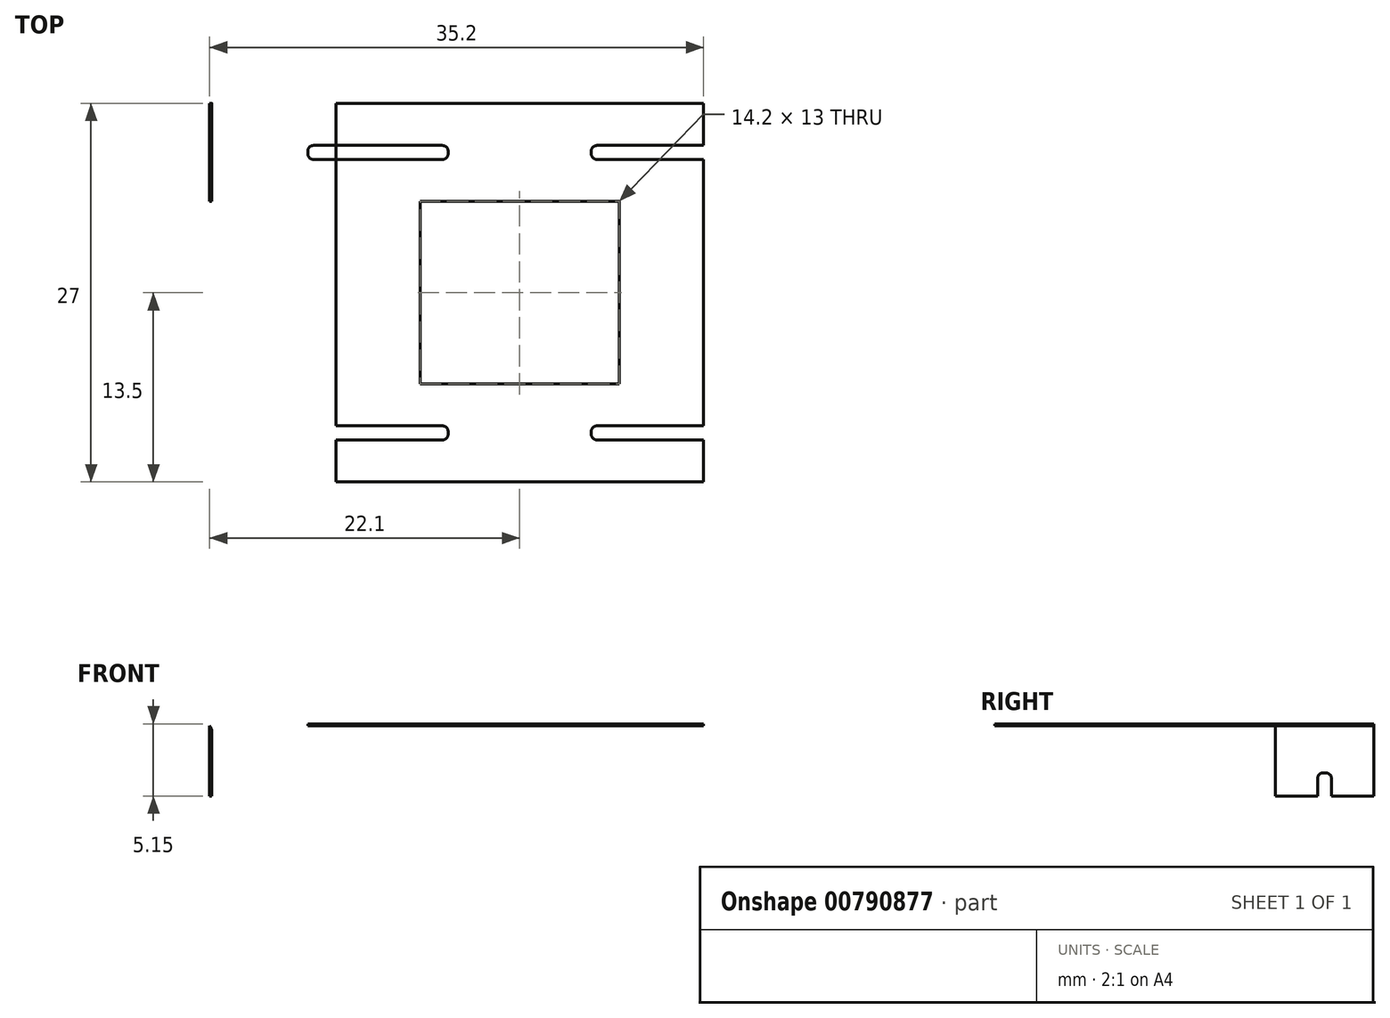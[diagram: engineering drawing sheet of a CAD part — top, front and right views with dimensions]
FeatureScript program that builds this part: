
annotation { "Feature Type Name" : "Feature", "Feature Type Description" : "" }
export const myFeature = defineFeature(function(context is Context, id is Id, definition is map)
    precondition{}
    {
        {
            var Q0;
            Q0=qCreatedBy(makeId("Top.planeOp"),FACE);
            var sketch = newSketch(context, id + "F0", { "sketchPlane" : qUnion([Q0])});
            skLineSegment(sketch, "E0.bottom", {"start": v(7.1, 6.5) * mm, "end": v(-7.1, 6.5) * mm});
            skLineSegment(sketch, "E0.top", {"start": v(7.1, -6.5) * mm, "end": v(-7.1, -6.5) * mm});
            skLineSegment(sketch, "E0.left", {"start": v(7.1, 6.5) * mm, "end": v(7.1, -6.5) * mm});
            skLineSegment(sketch, "E0.right", {"start": v(-7.1, 6.5) * mm, "end": v(-7.1, -6.5) * mm});
            skPoint(sketch, "E0.middle", {"position": v(0, 0) * mm});
            skLineSegment(sketch, "E1", {"start": v(13.1, 13.5) * mm, "end": v(13.1, 10.5) * mm});
            skLineSegment(sketch, "E2", {"start": v(13.1, 13.5) * mm, "end": v(-7.1, 13.5) * mm});
            skLineSegment(sketch, "E3.bottom", {"start": v(5.5, 9.5) * mm, "end": v(14.7, 9.5) * mm});
            skLineSegment(sketch, "E3.top", {"start": v(5.5, 10.5) * mm, "end": v(14.7, 10.5) * mm});
            skLineSegment(sketch, "E3.left", {"start": v(5.1, 9.9) * mm, "end": v(5.1, 10.1) * mm});
            skLineSegment(sketch, "E3.right", {"start": v(15.1, 9.9) * mm, "end": v(15.1, 10.1) * mm});
            skPoint(sketch, "E3.middle", {"position": v(10.1, 10) * mm});
            skPoint(sketch, "E4.visualSharp", {"position": v(5.1, 10.5) * mm});
            skArc(sketch, "E4.filletArc", {"start": v(5.5, 10.5) * mm, "mid": v(5.22, 10.38) * mm, "end": v(5.1, 10.1) * mm});
            skPoint(sketch, "E5.visualSharp", {"position": v(5.1, 9.5) * mm});
            skArc(sketch, "E5.filletArc", {"start": v(5.1, 9.9) * mm, "mid": v(5.22, 9.62) * mm, "end": v(5.5, 9.5) * mm});
            skPoint(sketch, "E6.visualSharp", {"position": v(15.1, 10.5) * mm});
            skArc(sketch, "E6.filletArc", {"start": v(15.1, 10.1) * mm, "mid": v(14.98, 10.38) * mm, "end": v(14.7, 10.5) * mm});
            skPoint(sketch, "E7.visualSharp", {"position": v(15.1, 9.5) * mm});
            skArc(sketch, "E7.filletArc", {"start": v(14.7, 9.5) * mm, "mid": v(14.98, 9.62) * mm, "end": v(15.1, 9.9) * mm});
            skLineSegment(sketch, "E8.trimOffspring", {"start": v(13.1, 9.5) * mm, "end": v(13.1, 0) * mm});
            skArc(sketch, "E9.MirrorCS", {"start": v(-5.5, 10.5) * mm, "mid": v(-5.22, 10.38) * mm, "end": v(-5.1, 10.1) * mm});
            skArc(sketch, "E10.MirrorCS", {"start": v(-15.1, 10.1) * mm, "mid": v(-14.98, 10.38) * mm, "end": v(-14.7, 10.5) * mm});
            skLineSegment(sketch, "E11.MirrorCS", {"start": v(-15.1, 9.9) * mm, "end": v(-15.1, 10.1) * mm});
            skArc(sketch, "E12.MirrorCS", {"start": v(-14.7, 9.5) * mm, "mid": v(-14.98, 9.62) * mm, "end": v(-15.1, 9.9) * mm});
            skArc(sketch, "E13.MirrorCS", {"start": v(-5.1, 9.9) * mm, "mid": v(-5.22, 9.62) * mm, "end": v(-5.5, 9.5) * mm});
            skLineSegment(sketch, "E14.MirrorCS", {"start": v(-5.1, 9.9) * mm, "end": v(-5.1, 10.1) * mm});
            skPoint(sketch, "E15.MirrorP", {"position": v(-5.1, 9.5) * mm});
            skLineSegment(sketch, "E16.MirrorCS", {"start": v(-5.5, 10.5) * mm, "end": v(-14.7, 10.5) * mm});
            skPoint(sketch, "E17.MirrorP", {"position": v(-10.1, 10) * mm});
            skLineSegment(sketch, "E18.MirrorCS", {"start": v(-5.5, 9.5) * mm, "end": v(-14.7, 9.5) * mm});
            skPoint(sketch, "E19.MirrorP", {"position": v(-15.1, 10.5) * mm});
            skLineSegment(sketch, "E20.MirrorCS", {"start": v(-13.1, 9.5) * mm, "end": v(-13.1, 0) * mm});
            skPoint(sketch, "E21.MirrorP", {"position": v(-5.1, 10.5) * mm});
            skLineSegment(sketch, "E22.MirrorCS", {"start": v(-13.1, 13.5) * mm, "end": v(-13.1, 10.5) * mm});
            skPoint(sketch, "E23.MirrorP", {"position": v(-15.1, 9.5) * mm});
            skLineSegment(sketch, "E24", {"start": v(-13.1, 13.5) * mm, "end": v(-7.1, 13.5) * mm});
            skLineSegment(sketch, "E25.bottom", {"start": v(-13.1, 13.5) * mm, "end": v(-22.1, 13.5) * mm});
            skLineSegment(sketch, "E25.top", {"start": v(-13.1, 6.5) * mm, "end": v(-22.1, 6.5) * mm});
            skLineSegment(sketch, "E25.left", {"start": v(-13.1, 13.5) * mm, "end": v(-13.1, 6.5) * mm});
            skLineSegment(sketch, "E25.right", {"start": v(-22.1, 13.5) * mm, "end": v(-22.1, 6.5) * mm});
            skArc(sketch, "E26.MirrorCS", {"start": v(14.7, -9.5) * mm, "mid": v(14.98, -9.62) * mm, "end": v(15.1, -9.9) * mm});
            skLineSegment(sketch, "E27.MirrorCS", {"start": v(15.1, -9.9) * mm, "end": v(15.1, -10.1) * mm});
            skArc(sketch, "E28.MirrorCS", {"start": v(15.1, -10.1) * mm, "mid": v(14.98, -10.38) * mm, "end": v(14.7, -10.5) * mm});
            skLineSegment(sketch, "E29.MirrorCS", {"start": v(13.1, -13.5) * mm, "end": v(13.1, -10.5) * mm});
            skLineSegment(sketch, "E30.MirrorCS", {"start": v(13.1, -9.5) * mm, "end": v(13.1, 0) * mm});
            skLineSegment(sketch, "E31.MirrorCS", {"start": v(13.1, -13.5) * mm, "end": v(-7.1, -13.5) * mm});
            skLineSegment(sketch, "E32.MirrorCS", {"start": v(5.5, -10.5) * mm, "end": v(14.7, -10.5) * mm});
            skPoint(sketch, "E33.MirrorP", {"position": v(15.1, -9.5) * mm});
            skPoint(sketch, "E34.MirrorP", {"position": v(15.1, -10.5) * mm});
            skPoint(sketch, "E35.MirrorP", {"position": v(10.1, -10) * mm});
            skLineSegment(sketch, "E36.MirrorCS", {"start": v(5.5, -9.5) * mm, "end": v(14.7, -9.5) * mm});
            skLineSegment(sketch, "E37.MirrorCS", {"start": v(5.1, -9.9) * mm, "end": v(5.1, -10.1) * mm});
            skArc(sketch, "E38.MirrorCS", {"start": v(5.1, -9.9) * mm, "mid": v(5.22, -9.62) * mm, "end": v(5.5, -9.5) * mm});
            skArc(sketch, "E39.MirrorCS", {"start": v(5.5, -10.5) * mm, "mid": v(5.22, -10.38) * mm, "end": v(5.1, -10.1) * mm});
            skPoint(sketch, "E40.MirrorP", {"position": v(5.1, -10.5) * mm});
            skPoint(sketch, "E41.MirrorP", {"position": v(5.1, -9.5) * mm});
            skArc(sketch, "E42.MirrorCS", {"start": v(-5.1, -9.9) * mm, "mid": v(-5.22, -9.62) * mm, "end": v(-5.5, -9.5) * mm});
            skArc(sketch, "E43.MirrorCS", {"start": v(-5.5, -10.5) * mm, "mid": v(-5.22, -10.38) * mm, "end": v(-5.1, -10.1) * mm});
            skLineSegment(sketch, "E44.MirrorCS", {"start": v(-5.1, -9.9) * mm, "end": v(-5.1, -10.1) * mm});
            skPoint(sketch, "E45.MirrorP", {"position": v(-5.1, -10.5) * mm});
            skLineSegment(sketch, "E46.MirrorCS", {"start": v(-5.5, -10.5) * mm, "end": v(-13.1, -10.5) * mm});
            skPoint(sketch, "E47.MirrorP", {"position": v(-10.1, -10) * mm});
            skPoint(sketch, "E48.MirrorP", {"position": v(-5.1, -9.5) * mm});
            skLineSegment(sketch, "E49.MirrorCS", {"start": v(-5.5, -9.5) * mm, "end": v(-13.1, -9.5) * mm});
            skLineSegment(sketch, "E50.MirrorCS", {"start": v(-13.1, -13.5) * mm, "end": v(-13.1, -10.5) * mm});
            skLineSegment(sketch, "E51.MirrorCS", {"start": v(-13.1, -13.5) * mm, "end": v(-7.1, -13.5) * mm});
            skLineSegment(sketch, "E52.MirrorCS", {"start": v(-13.1, -9.5) * mm, "end": v(-13.1, 0) * mm});
            skLineSegment(sketch, "E53.direction1", {"start": v(-7.1, -13.5) * mm, "end": v(13.1, -13.5) * mm, "construction": true});
            skPoint(sketch, "E54.orphan", {"position": v(-14.7, -9.5) * mm});
            skPoint(sketch, "E55.orphan", {"position": v(-14.7, -10.5) * mm});
            skLineSegment(sketch, "E56.trimOffspring", {"start": v(-13.1, -9.5) * mm, "end": v(-13.1, -6.5) * mm});
            skSolve(sketch);
        }
        {
            var Q0;
            {var subQ5=sQuery(id+"F0.wireOp",EDGE,"E10.MirrorCS");Q0=makeQuery(id+"F0.imprint","IMPRINT",FACE,{"disambiguationData":[TD([[makeQuery(id+"F0.imprint","IMPRINT",EDGE,{"derivedFrom":subQ5}),1.0]])]});}
            var Q1;
            {var subQ14=sQuery(id+"F0.wireOp",EDGE,"E53.1.0.0");Q1=makeQuery(id+"F0.imprint","IMPRINT",FACE,{"disambiguationData":[TD([[makeQuery(id+"F0.imprint","IMPRINT",EDGE,{"derivedFrom":subQ14}),1.0]])]});}
            var Q2;
            Q2=makeQuery(id+"F0.imprint","IMPRINT",FACE,{"disambiguationData":[TD([[makeQuery(id+"F0.imprint","IMPRINT",EDGE,{"derivedFrom":sQuery(id+"F0.wireOp",EDGE,"E0.bottom")}),-1.0]])]});
            var Q3;
            {var subQ5=sQuery(id+"F0.wireOp",EDGE,"E1");Q3=makeQuery(id+"F0.imprint","IMPRINT",FACE,{"disambiguationData":[TD([[makeQuery(id+"F0.imprint","IMPRINT",EDGE,{"derivedFrom":subQ5}),1.0]])]});}
            extrude(context, id + "F1", {"entities" : qUnion([Q0, Q1, Q2, Q3]), "depth" : 0.15 * mm, "offsetDistance" : 25 * mm});
        }
        {
            var Q0;
            Q0=makeQuery(id+"F1.opExtrude","CAP_FACE",FACE,{"disambiguationData":[OSD([sQuery(id+"F0.wireOp",EDGE,"E0.bottom"),sQuery(id+"F0.wireOp",EDGE,"E0.top"),sQuery(id+"F0.wireOp",EDGE,"E0.left"),sQuery(id+"F0.wireOp",EDGE,"E0.right"),sQuery(id+"F0.wireOp",EDGE,"E2"),sQuery(id+"F0.wireOp",EDGE,"E3.bottom"),sQuery(id+"F0.wireOp",EDGE,"E3.top"),sQuery(id+"F0.wireOp",EDGE,"E3.left"),sQuery(id+"F0.wireOp",EDGE,"E3.right"),sQuery(id+"F0.wireOp",EDGE,"E4.filletArc"),sQuery(id+"F0.wireOp",EDGE,"E5.filletArc"),sQuery(id+"F0.wireOp",EDGE,"E6.filletArc"),sQuery(id+"F0.wireOp",EDGE,"E7.filletArc"),sQuery(id+"F0.wireOp",EDGE,"E9.MirrorCS"),sQuery(id+"F0.wireOp",EDGE,"E10.MirrorCS"),sQuery(id+"F0.wireOp",EDGE,"E11.MirrorCS"),sQuery(id+"F0.wireOp",EDGE,"E12.MirrorCS"),sQuery(id+"F0.wireOp",EDGE,"E13.MirrorCS"),sQuery(id+"F0.wireOp",EDGE,"E14.MirrorCS"),sQuery(id+"F0.wireOp",EDGE,"E16.MirrorCS"),sQuery(id+"F0.wireOp",EDGE,"E18.MirrorCS"),sQuery(id+"F0.wireOp",EDGE,"E20.MirrorCS"),sQuery(id+"F0.wireOp",EDGE,"E24"),sQuery(id+"F0.wireOp",EDGE,"E25.bottom"),sQuery(id+"F0.wireOp",EDGE,"E25.top"),sQuery(id+"F0.wireOp",EDGE,"E25.right"),sQuery(id+"F0.wireOp",EDGE,"E26.MirrorCS"),sQuery(id+"F0.wireOp",EDGE,"E27.MirrorCS"),sQuery(id+"F0.wireOp",EDGE,"E28.MirrorCS"),sQuery(id+"F0.wireOp",EDGE,"E31.MirrorCS"),sQuery(id+"F0.wireOp",EDGE,"E32.MirrorCS"),sQuery(id+"F0.wireOp",EDGE,"E36.MirrorCS"),sQuery(id+"F0.wireOp",EDGE,"E37.MirrorCS"),sQuery(id+"F0.wireOp",EDGE,"E38.MirrorCS"),sQuery(id+"F0.wireOp",EDGE,"E39.MirrorCS"),sQuery(id+"F0.wireOp",EDGE,"E42.MirrorCS"),sQuery(id+"F0.wireOp",EDGE,"E43.MirrorCS"),sQuery(id+"F0.wireOp",EDGE,"E44.MirrorCS"),sQuery(id+"F0.wireOp",EDGE,"E46.MirrorCS"),sQuery(id+"F0.wireOp",EDGE,"E49.MirrorCS"),sQuery(id+"F0.wireOp",EDGE,"E50.MirrorCS"),sQuery(id+"F0.wireOp",EDGE,"E51.MirrorCS"),sQuery(id+"F0.wireOp",EDGE,"E52.MirrorCS"),sQuery(id+"F0.wireOp",EDGE,"E53.1.0.3"),sQuery(id+"F0.wireOp",EDGE,"E53.1.0.5"),sQuery(id+"F0.wireOp",EDGE,"E53.1.0.6"),sQuery(id+"F0.wireOp",EDGE,"E53.1.0.7"),sQuery(id+"F0.wireOp",EDGE,"E53.1.0.10"),sQuery(id+"F0.wireOp",EDGE,"E53.1.0.13"),sQuery(id+"F0.wireOp",EDGE,"E53.1.0.17"),sQuery(id+"F0.wireOp",EDGE,"E53.1.0.18"),sQuery(id+"F0.wireOp",EDGE,"E53.1.0.20"),sQuery(id+"F0.wireOp",EDGE,"E53.1.0.25"),sQuery(id+"F0.wireOp",EDGE,"E53.1.0.26"),sQuery(id+"F0.wireOp",EDGE,"E53.1.0.27"),sQuery(id+"F0.wireOp",EDGE,"E53.1.0.28"),sQuery(id+"F0.wireOp",EDGE,"E53.1.0.29"),sQuery(id+"F0.wireOp",EDGE,"E53.1.0.30"),sQuery(id+"F0.wireOp",EDGE,"E53.1.0.31"),sQuery(id+"F0.wireOp",EDGE,"E53.1.0.32"),sQuery(id+"F0.wireOp",EDGE,"E53.1.0.33"),sQuery(id+"F0.wireOp",EDGE,"E53.1.0.34"),sQuery(id+"F0.wireOp",EDGE,"E53.1.0.35"),sQuery(id+"F0.wireOp",EDGE,"E53.1.0.36"),sQuery(id+"F0.wireOp",EDGE,"E53.1.0.37"),sQuery(id+"F0.wireOp",EDGE,"E53.2.0.0"),sQuery(id+"F0.wireOp",EDGE,"E53.2.0.2"),sQuery(id+"F0.wireOp",EDGE,"E53.2.0.3"),sQuery(id+"F0.wireOp",EDGE,"E53.2.0.5"),sQuery(id+"F0.wireOp",EDGE,"E53.2.0.6"),sQuery(id+"F0.wireOp",EDGE,"E53.2.0.7"),sQuery(id+"F0.wireOp",EDGE,"E53.2.0.10"),sQuery(id+"F0.wireOp",EDGE,"E53.2.0.13"),sQuery(id+"F0.wireOp",EDGE,"E53.2.0.15"),sQuery(id+"F0.wireOp",EDGE,"E53.2.0.16"),sQuery(id+"F0.wireOp",EDGE,"E53.2.0.17"),sQuery(id+"F0.wireOp",EDGE,"E53.2.0.18"),sQuery(id+"F0.wireOp",EDGE,"E53.2.0.20"),sQuery(id+"F0.wireOp",EDGE,"E53.2.0.27"),sQuery(id+"F0.wireOp",EDGE,"E53.2.0.28"),sQuery(id+"F0.wireOp",EDGE,"E53.2.0.30"),sQuery(id+"F0.wireOp",EDGE,"E53.2.0.31"),sQuery(id+"F0.wireOp",EDGE,"E53.2.0.32"),sQuery(id+"F0.wireOp",EDGE,"E53.2.0.36"),sQuery(id+"F0.wireOp",EDGE,"E53.2.0.37"),sQuery(id+"F0.wireOp",EDGE,"E56.trimOffspring")])],"isStart":true});
            var sketch = newSketch(context, id + "F2", { "sketchPlane" : qUnion([Q0])});
            skLineSegment(sketch, "E57.bottom", {"start": v(-22.1, -13.5) * mm, "end": v(-21.95, -13.5) * mm});
            skLineSegment(sketch, "E57.top", {"start": v(-22.1, -6.5) * mm, "end": v(-21.95, -6.5) * mm});
            skLineSegment(sketch, "E57.left", {"start": v(-22.1, -13.5) * mm, "end": v(-22.1, -6.5) * mm});
            skLineSegment(sketch, "E57.right", {"start": v(-21.95, -13.5) * mm, "end": v(-21.95, -6.5) * mm});
            skSolve(sketch);
        }
        {
            var Q0;
            Q0=qSketchRegion(id+"F2",true);
            extrude(context, id + "F3", {"entities" : qUnion([Q0]), "operationType" : NewBodyOperationType.ADD, "depth" : 5 * mm, "offsetDistance" : 25 * mm});
        }
        {
            var Q0;
            Q0=makeQuery(id+"F3.opExtrude","CAP_EDGE",EDGE,{"disambiguationData":[OSD([sQuery(id+"F2.wireOp",EDGE,"E57.right")])],"isStart":true});
            var Q1;
            Q1=makeQuery(id+"F1.opExtrude","CAP_EDGE",EDGE,{"disambiguationData":[OSD([sQuery(id+"F0.wireOp",EDGE,"E25.right")])],"isStart":false});
            fillet(context, id + "F4", {"entities" : qUnion([Q0, Q1]), "radius" : 0.5 * mm, "tangentPropagation" : true, "allowEdgeOverflow" : false});
        }
        {
            var Q0;
            Q0=makeQuery(id+"F3.boolean.opBoolean","MERGE",FACE,{"derivedFrom":[makeQuery(id+"F1.opExtrude","SWEPT_FACE",FACE,{"disambiguationData":[OSD([sQuery(id+"F0.wireOp",EDGE,"E25.right")])]}),makeQuery(id+"F3.opExtrude","SWEPT_FACE",FACE,{"disambiguationData":[OSD([sQuery(id+"F2.wireOp",EDGE,"E57.left")])]})]});
            var sketch = newSketch(context, id + "F5", { "sketchPlane" : qUnion([Q0])});
            skLineSegment(sketch, "E58", {"start": v(-10, -0.35) * mm, "end": v(-10, -3.35) * mm});
            skLineSegment(sketch, "E59", {"start": v(-10, -3.35) * mm, "end": v(-9.9, -3.35) * mm});
            skLineSegment(sketch, "E60", {"start": v(-9.5, -3.75) * mm, "end": v(-9.5, -5) * mm});
            skPoint(sketch, "E61.visualSharp", {"position": v(-9.5, -3.35) * mm});
            skArc(sketch, "E61.filletArc", {"start": v(-9.5, -3.75) * mm, "mid": v(-9.62, -3.47) * mm, "end": v(-9.9, -3.35) * mm});
            skPoint(sketch, "E62.MirrorP", {"position": v(-10.5, -3.35) * mm});
            skLineSegment(sketch, "E63.MirrorCS", {"start": v(-10.5, -3.75) * mm, "end": v(-10.5, -5) * mm});
            skArc(sketch, "E64.MirrorCS", {"start": v(-10.5, -3.75) * mm, "mid": v(-10.38, -3.47) * mm, "end": v(-10.1, -3.35) * mm});
            skLineSegment(sketch, "E65.MirrorCS", {"start": v(-10, -3.35) * mm, "end": v(-10.1, -3.35) * mm});
            skSolve(sketch);
        }
        {
            var Q0;
            Q0=makeQuery(id+"F5.imprint","IMPRINT",FACE,{"disambiguationData":[TD([[makeQuery(id+"F5.imprint","IMPRINT",EDGE,{"derivedFrom":sQuery(id+"F5.wireOp",EDGE,"E59")}),-1.0]])]});
            extrude(context, id + "F6", {"entities" : qUnion([Q0]), "operationType" : NewBodyOperationType.REMOVE, "oppositeDirection" : true, "depth" : 25 * mm, "offsetDistance" : 25 * mm});
        }
    });
